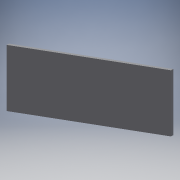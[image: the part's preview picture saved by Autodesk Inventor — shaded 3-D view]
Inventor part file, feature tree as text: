
AUTODESK INVENTOR PART (.ipt)
format: ipt  version: 2018.3 (Build 223284000, 284)  size: 4,371,968 bytes
history: native  units: mm
features: extrude x3, sketch x3, pattern_linear x2
ambient origin geometry x8: Origin, YZ Plane, XZ Plane, XY Plane, X Axis, Y Axis, Z Axis, Center Point
bodies: Solid1 (feature_tree)
feature tree (8):
  extrude  "Extrusion1"  Depth=2.0mm
  extrude  "Extrusion2"  Depth=3.0mm
  extrude  "Extrusion3"  Depth=1.0mm
  pattern_linear  "Rectangular Pattern1"  Spacing1=1.0mm  [1 undecoded]
  pattern_linear  "Rectangular Pattern2"  Spacing1=0.2mm  [1 undecoded]
  sketch  "Sketch1"  dims[d0=105.0mm d1=2.0mm]
  sketch  "Sketch2"  dims[d2=50.0mm d3=0.0mm d4=3.0mm]
  sketch  "Sketch3"  dims[d5=3.0mm d27=1.0mm d40=1.0mm d41=0.2mm d42=0.4mm d43=0.2mm d44=0.4mm d45=0.1mm d46=0.0mm d47=0.03mm d48=0.02mm d49=0.001mm d50=0.0mm d51=140.0mm d53=3.5mm d54=300.0mm d56=3.45mm]
note: 2 required parameter values undecoded (feature->parameter linkage not recoverable at this tier; creation-order binding heuristic only, values carry confidence <= 0.55)
